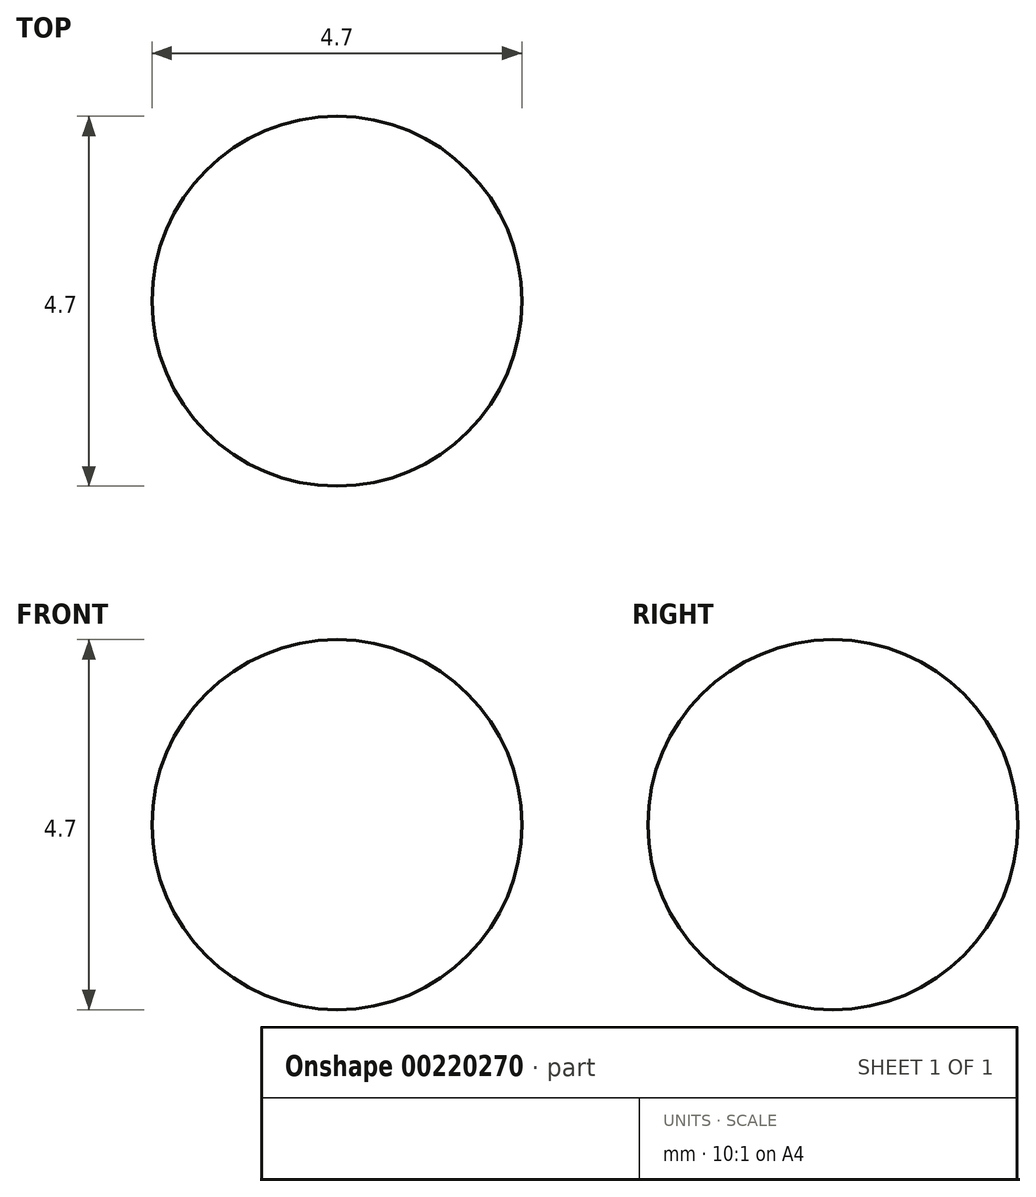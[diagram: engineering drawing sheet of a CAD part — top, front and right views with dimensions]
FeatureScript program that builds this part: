
annotation { "Feature Type Name" : "Feature", "Feature Type Description" : "" }
export const myFeature = defineFeature(function(context is Context, id is Id, definition is map)
    precondition{}
    {
        {
            var Q0;
            Q0=qCreatedBy(makeId("Front.planeOp"),FACE);
            var sketch = newSketch(context, id + "F0", { "sketchPlane" : qUnion([Q0])});
            skCircle(sketch, "E0", {"center": v(0, 0) * mm, "radius": 2.35 * mm, "construction": true});
            skArc(sketch, "E1", {"start": v(0, -2.35) * mm, "mid": v(2.35, 0) * mm, "end": v(0, 2.35) * mm});
            skLineSegment(sketch, "E2", {"start": v(0, 2.35) * mm, "end": v(0, -2.35) * mm});
            skSolve(sketch);
        }
        {
            var Q0;
            Q0=makeQuery(id+"F0.imprint","IMPRINT",FACE,{"disambiguationData":[TD([[makeQuery(id+"F0.imprint","IMPRINT",EDGE,{"derivedFrom":sQuery(id+"F0.wireOp",EDGE,"E1")}),1.0]])]});
            var Q1;
            Q1=sQuery(id+"F0.wireOp",EDGE,"E2");
            revolve(context, id + "F1", {"entities" : qUnion([Q0]), "axis" : qUnion([Q1]), "revolveType" : RevolveType.FULL});
        }
    });
